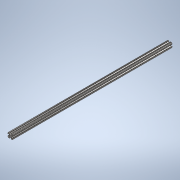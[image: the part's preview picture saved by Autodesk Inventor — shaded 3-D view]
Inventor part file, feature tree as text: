
AUTODESK INVENTOR PART (.ipt)
format: ipt  version: 2020 (Build 240168000, 168)  size: 245,248 bytes
history: native  units: in
note: dims shown in document units (in); Inventor stores cm internally (conversion verified against a paired STEP export)
features: extrude x1, sketch x1
ambient origin geometry x8: Origin, YZ Plane, XZ Plane, XY Plane, X Axis, Y Axis, Z Axis, Center Point
bodies: Solid1 (feature_tree)
feature tree (2):
  extrude  "Extrusion1"  [1 undecoded]
  sketch  "Sketch1"  dims[d0=34.0in d1=0.0in]
note: 1 required parameter value undecoded (feature->parameter linkage not recoverable at this tier; creation-order binding heuristic only, values carry confidence <= 0.55)
